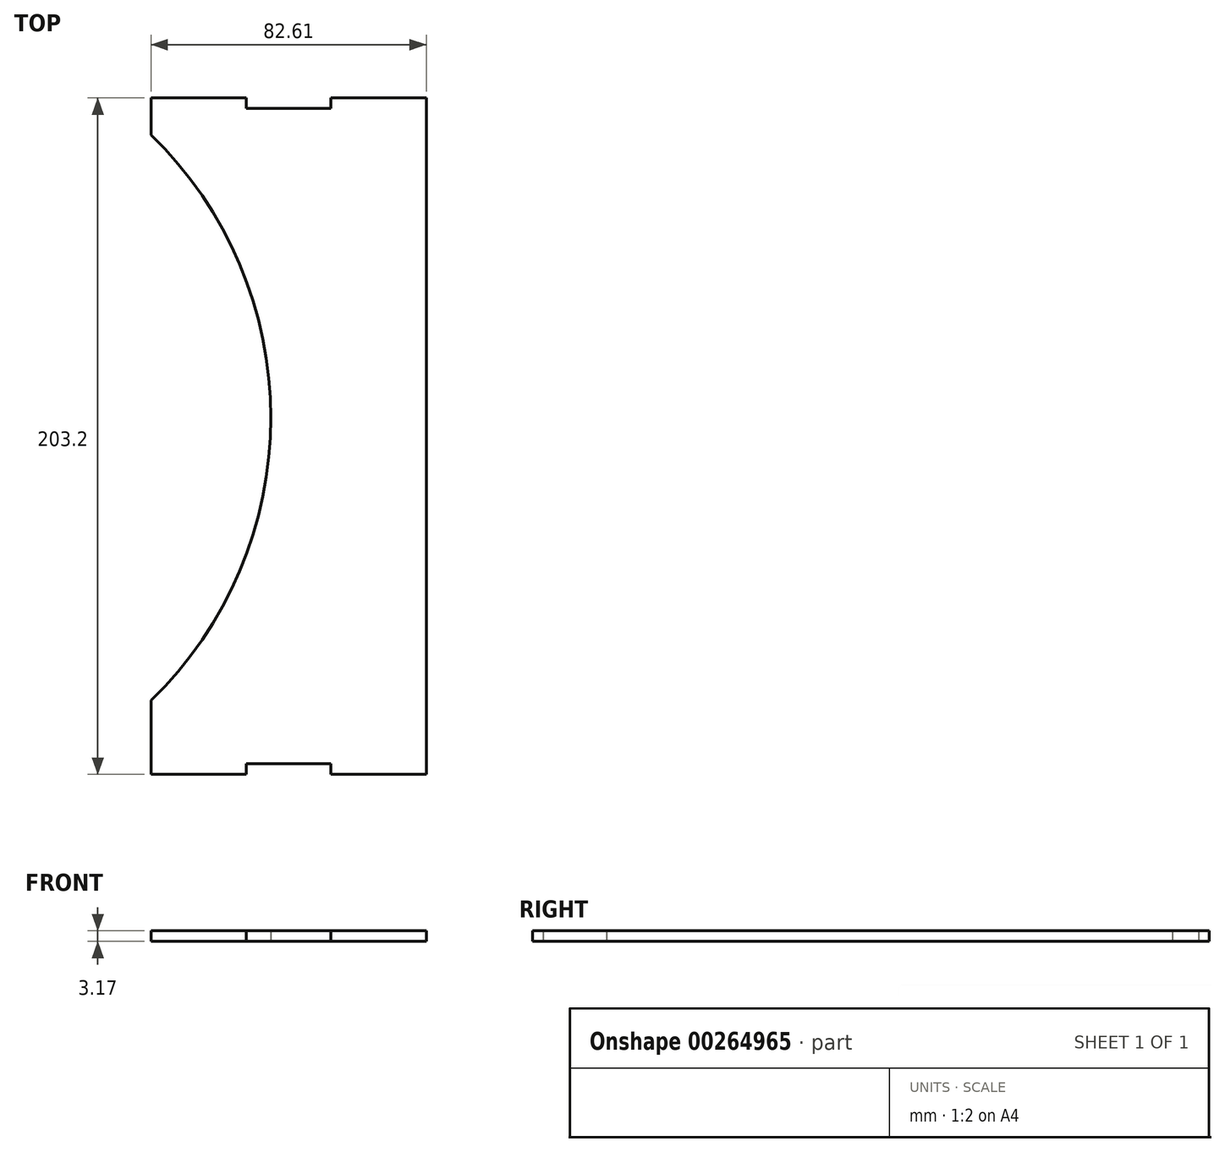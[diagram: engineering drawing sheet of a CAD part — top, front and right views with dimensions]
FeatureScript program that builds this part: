
annotation { "Feature Type Name" : "Feature", "Feature Type Description" : "" }
export const myFeature = defineFeature(function(context is Context, id is Id, definition is map)
    precondition{}
    {
        {
            var Q0;
            Q0=qCreatedBy(makeId("Top.planeOp"),FACE);
            var sketch = newSketch(context, id + "F0", { "sketchPlane" : qUnion([Q0])});
            skLineSegment(sketch, "E0", {"start": v(-42.96, -101.6) * mm, "end": v(-42.96, -79.38) * mm});
            skLineSegment(sketch, "E1.trimOffspring", {"start": v(14.02, -101.6) * mm, "end": v(39.65, -101.6) * mm});
            skLineSegment(sketch, "E2.MirrorCS", {"start": v(-42.96, 101.6) * mm, "end": v(-14.91, 101.6) * mm});
            skLineSegment(sketch, "E3.MirrorCS", {"start": v(13.77, 101.6) * mm, "end": v(39.65, 101.6) * mm});
            skPoint(sketch, "E4.visualSharp", {"position": v(-2.38, 0) * mm});
            skLineSegment(sketch, "E5", {"start": v(-42.07, 80.87) * mm, "end": v(-42.07, 79.46) * mm});
            skPoint(sketch, "E6.end.orphan", {"position": v(-2.38, 79.38) * mm});
            skPoint(sketch, "E7.start.orphan", {"position": v(-2.38, -79.38) * mm});
            skPoint(sketch, "E8.visualSharp", {"position": v(-42.07, 79.38) * mm});
            skArc(sketch, "E8.filletArc", {"start": v(-42.07, 79.46) * mm, "mid": v(-42.06, 79.38) * mm, "end": v(-42.02, 79.3) * mm});
            skPoint(sketch, "E9.endSnap0", {"position": v(27.8, 101.6) * mm});
            skPoint(sketch, "E10.end.orphan", {"position": v(42.07, 0) * mm});
            skLineSegment(sketch, "E11", {"start": v(39.53, -101.6) * mm, "end": v(39.65, -101.6) * mm});
            skPoint(sketch, "E9.end.orphan", {"position": v(38.64, 101.6) * mm});
            skLineSegment(sketch, "E12", {"start": v(-42.96, 101.6) * mm, "end": v(-42.96, 90.49) * mm});
            skPoint(sketch, "E13", {"position": v(-41.81, 5.52) * mm});
            skArc(sketch, "E14", {"start": v(-42.96, -79.38) * mm, "mid": v(-7.02, 5.56) * mm, "end": v(-42.96, 90.49) * mm});
            skPoint(sketch, "E15.MirrorCS.end.orphan", {"position": v(-13.77, 104.78) * mm});
            skPoint(sketch, "E15.MirrorCS.start.orphan", {"position": v(-14.02, 104.78) * mm});
            skPoint(sketch, "E16.orphan", {"position": v(41.81, 101.6) * mm});
            skPoint(sketch, "E17.orphan", {"position": v(-42.07, -104.78) * mm});
            skPoint(sketch, "E18.start.orphan", {"position": v(14.02, -104.78) * mm});
            skPoint(sketch, "E19.orphan", {"position": v(-42.07, 104.78) * mm});
            skLineSegment(sketch, "E20", {"start": v(-42.96, -101.6) * mm, "end": v(-14.66, -101.6) * mm});
            skPoint(sketch, "E21.start.orphan", {"position": v(0.13, -101.6) * mm});
            skLineSegment(sketch, "E22.trimOffspring", {"start": v(11.94, -101.6) * mm, "end": v(14.02, -101.6) * mm});
            skLineSegment(sketch, "E23", {"start": v(-0.76, 98.43) * mm, "end": v(-13.46, 98.43) * mm});
            skLineSegment(sketch, "E24", {"start": v(-0.76, 98.43) * mm, "end": v(11.05, 98.43) * mm});
            skLineSegment(sketch, "E25.trimOffspring", {"start": v(13.77, 101.6) * mm, "end": v(14.02, 101.6) * mm});
            skPoint(sketch, "E26.orphan", {"position": v(-0.76, 101.6) * mm});
            skLineSegment(sketch, "E27.trimOffspring", {"start": v(11.94, 101.6) * mm, "end": v(14.02, 101.6) * mm});
            skLineSegment(sketch, "E28", {"start": v(11.05, -98.43) * mm, "end": v(-13.46, -98.43) * mm});
            skPoint(sketch, "E29.start.orphan", {"position": v(-12.57, -98.42) * mm});
            skLineSegment(sketch, "E30", {"start": v(-14.91, 101.6) * mm, "end": v(-14.35, 101.6) * mm});
            skPoint(sketch, "E31.orphan", {"position": v(40.54, -101.6) * mm});
            skPoint(sketch, "E32.orphan", {"position": v(40.54, 101.6) * mm});
            skLineSegment(sketch, "E33", {"start": v(-13.46, 98.43) * mm, "end": v(-14.35, 98.43) * mm});
            skLineSegment(sketch, "E34", {"start": v(-14.35, 98.43) * mm, "end": v(-14.35, 101.6) * mm});
            skLineSegment(sketch, "E35", {"start": v(11.94, 101.6) * mm, "end": v(11.05, 101.6) * mm});
            skLineSegment(sketch, "E36", {"start": v(11.05, 101.6) * mm, "end": v(11.05, 98.43) * mm});
            skLineSegment(sketch, "E37", {"start": v(11.05, -98.43) * mm, "end": v(11.05, -101.6) * mm});
            skLineSegment(sketch, "E38", {"start": v(11.05, -101.6) * mm, "end": v(11.94, -101.6) * mm});
            skLineSegment(sketch, "E39", {"start": v(-14.35, -98.43) * mm, "end": v(-14.35, -101.6) * mm});
            skLineSegment(sketch, "E40", {"start": v(-13.46, -98.43) * mm, "end": v(-14.35, -98.43) * mm});
            skPoint(sketch, "E41.orphan", {"position": v(-13.46, -101.6) * mm});
            skLineSegment(sketch, "E42.trimOffspring", {"start": v(-14.35, -101.6) * mm, "end": v(-14.66, -101.6) * mm});
            skPoint(sketch, "E43.end.orphan", {"position": v(-13.77, -101.6) * mm});
            skLineSegment(sketch, "E44", {"start": v(39.65, 101.6) * mm, "end": v(39.65, -101.6) * mm});
            skSolve(sketch);
        }
        {
            var Q0;
            Q0=makeQuery(id+"F0.imprint","IMPRINT",FACE,{"disambiguationData":[TD([[makeQuery(id+"F0.imprint","IMPRINT",EDGE,{"derivedFrom":sQuery(id+"F0.wireOp",EDGE,"E0")}),-1.0]])]});
            extrude(context, id + "F1", {"entities" : qUnion([Q0]), "depth" : 3.17 * mm});
        }
    });
